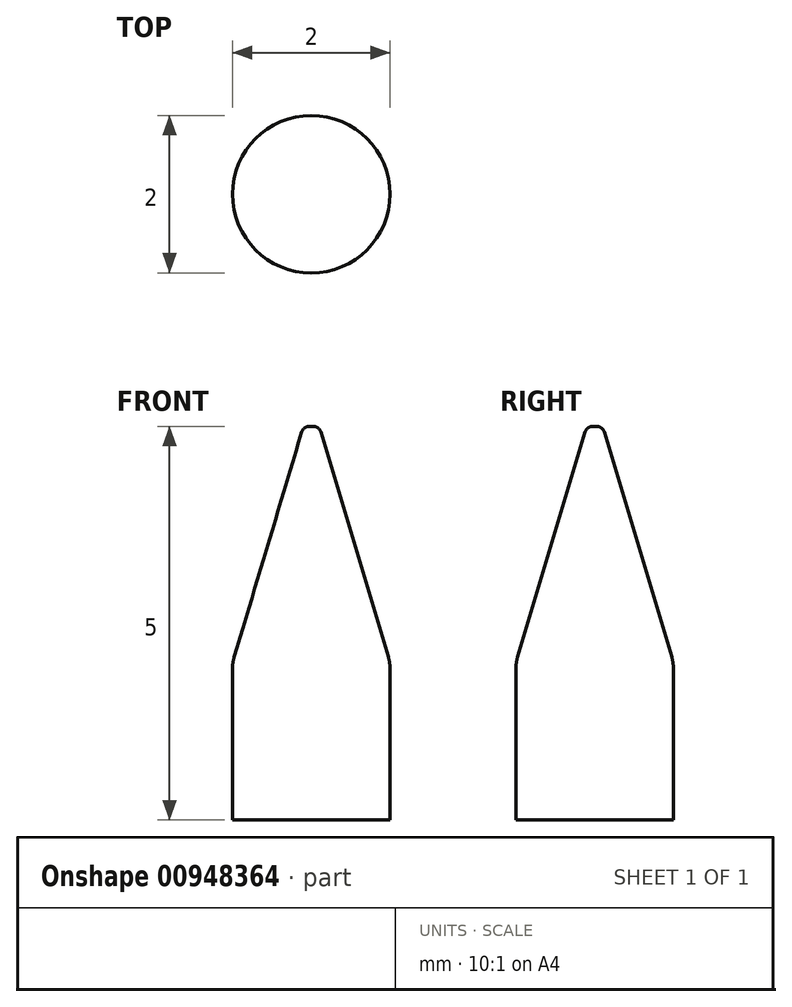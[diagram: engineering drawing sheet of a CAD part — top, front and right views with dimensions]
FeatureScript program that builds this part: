
annotation { "Feature Type Name" : "Feature", "Feature Type Description" : "" }
export const myFeature = defineFeature(function(context is Context, id is Id, definition is map)
    precondition{}
    {
        {
            var Q0;
            Q0=qCreatedBy(makeId("Front.planeOp"),FACE);
            var sketch = newSketch(context, id + "F0", { "sketchPlane" : qUnion([Q0])});
            skLineSegment(sketch, "E0", {"start": v(0, 0) * mm, "end": v(1, 0) * mm});
            skLineSegment(sketch, "E1", {"start": v(1, 0) * mm, "end": v(1, 2) * mm});
            skLineSegment(sketch, "E2", {"start": v(0, 5) * mm, "end": v(0, 0) * mm});
            skLineSegment(sketch, "E3", {"start": v(0, 5) * mm, "end": v(0.1, 5) * mm});
            skLineSegment(sketch, "E4", {"start": v(0.1, 5) * mm, "end": v(1, 2) * mm});
            skSolve(sketch);
        }
        {
            var Q0;
            Q0=makeQuery(id+"F0.imprint","IMPRINT",FACE,{"disambiguationData":[TD([[makeQuery(id+"F0.imprint","IMPRINT",EDGE,{"derivedFrom":sQuery(id+"F0.wireOp",EDGE,"E0")}),1.0]])]});
            var Q1;
            Q1=sQuery(id+"F0.wireOp",EDGE,"E2");
            revolve(context, id + "F1", {"surfaceOperationType" : NewSurfaceOperationType.NEW, "entities" : qUnion([Q0]), "axis" : qUnion([Q1]), "revolveType" : RevolveType.FULL});
        }
        {
            var Q0;
            Q0=makeQuery(id+"F1.opRevolve","SWEPT_EDGE",EDGE,{"disambiguationData":[OSD([sQuery(id+"F0.wireOp",EDGE,"E3"),sQuery(id+"F0.wireOp",EDGE,"E4")])]});
            fillet(context, id + "F2", {"entities" : qUnion([Q0]), "radius" : 0.1 * mm, "tangentPropagation" : true, "allowEdgeOverflow" : false});
        }
        {
            var Q0;
            Q0=makeQuery(id+"F1.opRevolve","SWEPT_EDGE",EDGE,{"disambiguationData":[OSD([sQuery(id+"F0.wireOp",EDGE,"E1"),sQuery(id+"F0.wireOp",EDGE,"E4")])]});
            fillet(context, id + "F3", {"entities" : qUnion([Q0]), "radius" : 0.5 * mm, "tangentPropagation" : true, "allowEdgeOverflow" : false});
        }
    });
